# Revit family: AVAB_Horizontal_Floor_Mount
name_source: partatom
category: Duct Fittings
units: mm (PartAtom-declared; Revit-internal decimal feet)

## family parameters
Always vertical = Yes
Cut with Voids When Loaded = No
Part Type = Elbow
Round Connector Dimension = Use Radius
Shared = No
Work Plane-Based = No

## types (8) — shared parameters
30 = 30.00°
60 = 60.00°
Four = 4 "
Manufacturer = Loren Cook Company
Model = AVAB
ONE EIGTH = 0.125 "
One = 1 "
Oneandahalf = 1.5 "
Three = 3 "
Twentyfour = 24 "
Two = 2 "
Type Comments = Adjustable Pitch Vane Axial Horizontal Floor Mount Belt Drive Arrangement 9
URL = www.lorencook.com
zero-valued in all types: Zero

## per-type parameters (varying)
- 35_AVAB_HOR_FLOOR: A=35.5 "; AThird=14.2 "; Ab=17.875 "; B=39.875 "; C=38 "; Ca=42 "; Cone_C=35.5 "; Cone_C_Rad=17.75 "; Cone_F=39.375 "; Cone_F_Rad=19.688 "; Cone_G=0.135 "; Cone_H=43.875 "; Cone_K=14.688 "; E=43 "; ELess2=41 "; Ea=-21.5 "; Eb=-21.375 "; Ec=21.375 "; F=0.563 "; FootWidth=3.25 "; G=144 "; H=35.125 "; Ha=17.375 "; HalfA=17.75 "; HalfB=19.938 "; HalfC=19 "; HalfE=21.5 "; HalfF=0.281 "; HalfJ=19.875 "; HalfM=20.5 "; HalfP=0.313 "; Hb=58.125 "; Hc=8.688 "; InnerFoot=36.5 "; J=39.75 "; K=1.625 "; L=23 "; La=4 "; M=41 "; N=12 "; P=0.625 "
- 39_AVAB_HOR_FLOOR: A=39.375 "; AThird=15.75 "; Ab=19.813 "; B=43.938 "; C=41.875 "; Ca=46.938 "; Cone_C=39.375 "; Cone_C_Rad=19.688 "; Cone_F=44.125 "; Cone_F_Rad=22.063 "; Cone_G=0.135 "; Cone_H=49.625 "; Cone_K=18 "; E=43 "; ELess2=41 "; Ea=-21.5 "; Eb=-21.375 "; Ec=21.375 "; F=0.563 "; FootWidth=3.5 "; G=144 "; H=37.125 "; Ha=17.438 "; HalfA=19.688 "; HalfB=21.969 "; HalfC=20.938 "; HalfE=21.5 "; HalfF=0.281 "; HalfJ=19.75 "; HalfM=22.5 "; HalfP=0.313 "; Hb=63.125 "; Hc=8.719 "; InnerFoot=36 "; J=39.5 "; K=1.75 "; L=26 "; La=5.063 "; M=45 "; N=13.375 "; P=0.625 "
- 44_AVAB_HOR_FLOOR: A=44.125 "; AThird=17.65 "; Ab=22.188 "; B=49.625 "; C=47.375 "; Ca=52.188 "; Cone_C=44.125 "; Cone_C_Rad=22.063 "; Cone_F=49.25 "; Cone_F_Rad=24.625 "; Cone_G=0.135 "; Cone_H=54.75 "; Cone_K=19.5 "; E=47 "; ELess2=45 "; Ea=-23.5 "; Eb=-23.375 "; Ec=23.375 "; F=0.563 "; FootWidth=3.5 "; G=144 "; H=42.625 "; Ha=20.563 "; HalfA=22.063 "; HalfB=24.813 "; HalfC=23.688 "; HalfE=23.5 "; HalfF=0.281 "; HalfJ=21.75 "; HalfM=25.5 "; HalfP=0.313 "; Hb=71.125 "; Hc=10.281 "; InnerFoot=40 "; J=43.5 "; K=1.75 "; L=28.5 "; La=4.813 "; M=51 "; N=15.375 "; P=0.625 "
- 49_AVAB_HOR_FLOOR: A=49.25 "; AThird=19.7 "; Ab=24.75 "; B=54.75 "; C=52.5 "; Ca=57.75 "; Cone_C=49.25 "; Cone_C_Rad=24.625 "; Cone_F=55.125 "; Cone_F_Rad=27.563 "; Cone_G=0.135 "; Cone_H=60.625 "; Cone_K=22.313 "; E=47 "; ELess2=45 "; Ea=-23.5 "; Eb=-23.375 "; Ec=23.375 "; F=0.563 "; FootWidth=3.5 "; G=144 "; H=43.563 "; Ha=18.938 "; HalfA=24.625 "; HalfB=27.375 "; HalfC=26.25 "; HalfE=23.5 "; HalfF=0.281 "; HalfJ=21.75 "; HalfM=28 "; HalfP=0.313 "; Hb=75.063 "; Hc=9.469 "; InnerFoot=40 "; J=43.5 "; K=1.75 "; L=31.5 "; La=5.25 "; M=56 "; N=17 "; P=0.625 "
- 57_AVAB_HOR_FLOOR: A=57.125 "; AThird=22.85 "; Ab=28.688 "; B=62.625 "; C=59.875 "; Ca=62.938 "; Cone_C=57.125 "; Cone_C_Rad=28.563 "; Cone_F=65 "; Cone_F_Rad=32.5 "; Cone_G=0.135 "; Cone_H=70.5 "; Cone_K=29.938 "; E=61 "; ELess2=59 "; Ea=-30.5 "; Eb=-30.375 "; Ec=30.375 "; F=0.563 "; FootWidth=3.5 "; G=144 "; H=44.625 "; Ha=16.063 "; HalfA=28.563 "; HalfB=31.313 "; HalfC=29.938 "; HalfE=30.5 "; HalfF=0.281 "; HalfJ=28.75 "; HalfM=34 "; HalfP=0.313 "; Hb=77.625 "; Hc=8.031 "; InnerFoot=54 "; J=57.5 "; K=1.75 "; L=33 "; La=3.063 "; M=68 "; N=21 "; P=0.625 "
- 63_AVAB_HOR_FLOOR: A=63 "; AThird=25.2 "; Ab=31.625 "; B=68.5 "; C=66.25 "; Ca=73.125 "; Cone_C=63 "; Cone_C_Rad=31.5 "; Cone_F=70.875 "; Cone_F_Rad=35.438 "; Cone_G=0.179 "; Cone_H=77.625 "; Cone_K=29.938 "; E=61 "; ELess2=59 "; Ea=-30.5 "; Eb=-30.375 "; Ec=30.375 "; F=0.688 "; FootWidth=3.5 "; G=192 "; H=46.75 "; Ha=15.25 "; HalfA=31.5 "; HalfB=34.25 "; HalfC=33.125 "; HalfE=30.5 "; HalfF=0.344 "; HalfJ=28.75 "; HalfM=35 "; HalfP=0.375 "; Hb=86.75 "; Hc=7.625 "; InnerFoot=54 "; J=57.5 "; K=1.75 "; L=40 "; La=6.875 "; M=70 "; N=21.625 "; P=0.75 "
- 71_AVAB_HOR_FLOOR: A=70.875 "; AThird=28.35 "; Ab=35.563 "; B=77.625 "; C=75 "; Ca=81.5 "; Cone_C=70.875 "; Cone_C_Rad=35.438 "; Cone_F=78.75 "; Cone_F_Rad=39.375 "; Cone_G=0.179 "; Cone_H=93.375 "; Cone_K=29.938 "; E=72 "; ELess2=70 "; Ea=-36 "; Eb=-35.875 "; Ec=35.875 "; F=0.688 "; FootWidth=4.5 "; G=192 "; H=64.25 "; Ha=28.813 "; HalfA=35.438 "; HalfB=38.813 "; HalfC=37.5 "; HalfE=36 "; HalfF=0.344 "; HalfJ=33.75 "; HalfM=39.25 "; HalfP=0.375 "; Hb=108.25 "; Hc=14.406 "; InnerFoot=63 "; J=67.5 "; K=2.25 "; L=44 "; La=6.5 "; M=78.5 "; N=24.375 "; P=0.75 "
- 79_AVAB_HOR_FLOOR: A=78.75 "; AThird=31.5 "; Ab=39.5 "; B=85.563 "; C=82.875 "; Ca=88.938 "; Cone_C=78.75 "; Cone_C_Rad=39.375 "; Cone_F=86.625 "; Cone_F_Rad=43.313 "; Cone_G=0.179 "; Cone_H=93.375 "; Cone_K=29.653 "; E=72 "; ELess2=70 "; Ea=-36 "; Eb=-35.875 "; Ec=35.875 "; F=0.688 "; FootWidth=4.5 "; G=192 "; H=67.25 "; Ha=27.875 "; HalfA=39.375 "; HalfB=42.781 "; HalfC=41.438 "; HalfE=36 "; HalfF=0.344 "; HalfJ=33.75 "; HalfM=43.5 "; HalfP=0.375 "; Hb=114.75 "; Hc=13.938 "; InnerFoot=63 "; J=67.5 "; K=2.25 "; L=47.5 "; La=6.063 "; M=87 "; N=27.375 "; P=0.75 "

## geometry (parser evidence)
native form markers: Blend x2, Sweep x3
no freeform markers — native parametric forms only
